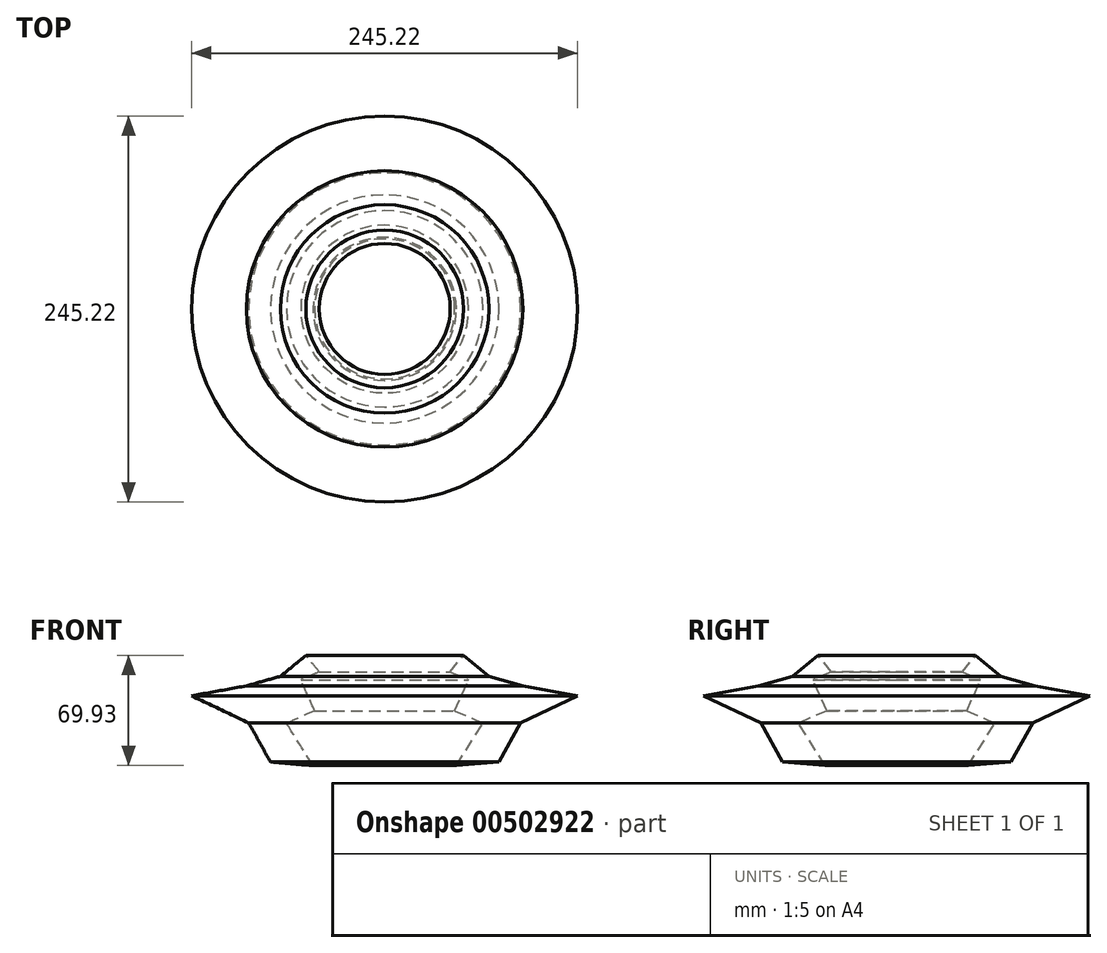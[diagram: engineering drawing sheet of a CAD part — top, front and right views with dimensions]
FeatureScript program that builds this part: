
annotation { "Feature Type Name" : "Feature", "Feature Type Description" : "" }
export const myFeature = defineFeature(function(context is Context, id is Id, definition is map)
    precondition{}
    {
        {
            var Q0;
            Q0=qCreatedBy(makeId("Front.planeOp"),FACE);
            var sketch = newSketch(context, id + "F0", { "sketchPlane" : qUnion([Q0])});
            skLineSegment(sketch, "E0", {"start": v(-66.2, 21.87) * mm, "end": v(-50.08, 35.11) * mm});
            skLineSegment(sketch, "E1", {"start": v(-50.08, 35.11) * mm, "end": v(-41.6, 24.78) * mm});
            skLineSegment(sketch, "E2", {"start": v(-41.6, 24.78) * mm, "end": v(-53.24, 19.57) * mm});
            skLineSegment(sketch, "E3", {"start": v(-53.24, 19.57) * mm, "end": v(-44.49, 0) * mm});
            skLineSegment(sketch, "E4", {"start": v(-44.49, 0) * mm, "end": v(-62.35, -8) * mm});
            skLineSegment(sketch, "E5", {"start": v(-62.35, -8) * mm, "end": v(-45.47, -34.82) * mm});
            skLineSegment(sketch, "E6", {"start": v(-45.47, -34.82) * mm, "end": v(-72.53, -32.52) * mm});
            skLineSegment(sketch, "E7", {"start": v(-72.53, -32.52) * mm, "end": v(-86.34, -7.77) * mm});
            skLineSegment(sketch, "E8", {"start": v(-86.34, -7.77) * mm, "end": v(-122.6, 9.5) * mm});
            skLineSegment(sketch, "E9", {"start": v(-122.6, 9.5) * mm, "end": v(-87.78, 15.83) * mm});
            skLineSegment(sketch, "E10", {"start": v(-87.78, 15.83) * mm, "end": v(-66.2, 21.87) * mm});
            skLineSegment(sketch, "E11", {"start": v(0, 0) * mm, "end": v(0, 27.34) * mm, "construction": true});
            skSolve(sketch);
        }
        {
            var Q0;
            Q0 = qSketchRegion(id + "F0", true);
            var Q1;
            Q1=sQuery(id+"F0.wireOp",EDGE,"E11");
            revolve(context, id + "F1", {"entities" : qUnion([Q0]), "axis" : qUnion([Q1]), "revolveType" : RevolveType.FULL});
        }
    });
